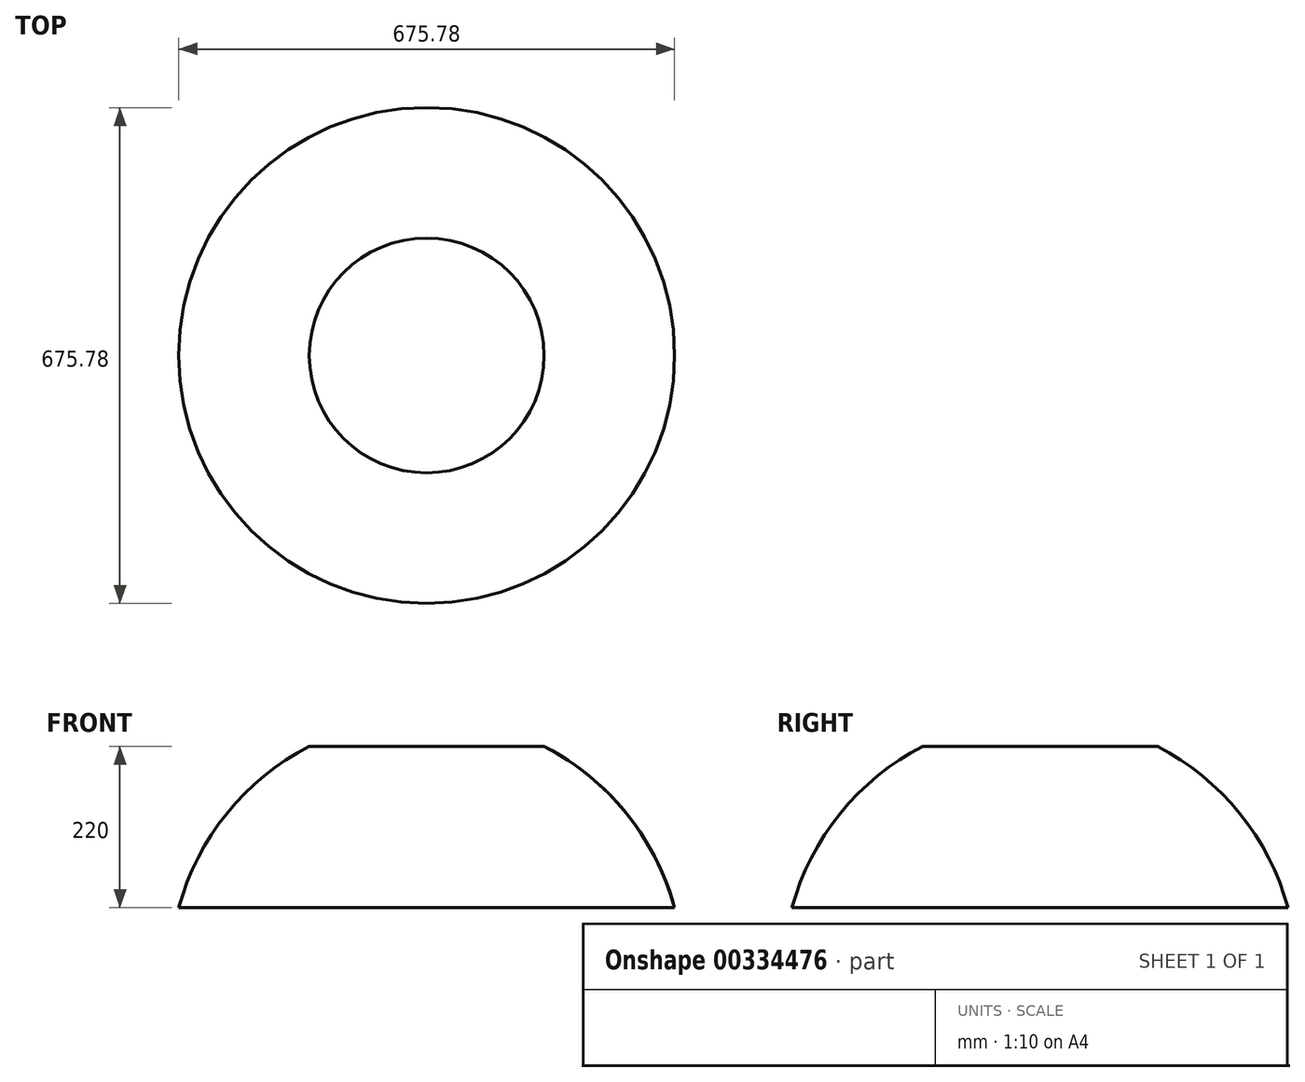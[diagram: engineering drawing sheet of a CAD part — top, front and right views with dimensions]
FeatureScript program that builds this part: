
annotation { "Feature Type Name" : "Feature", "Feature Type Description" : "" }
export const myFeature = defineFeature(function(context is Context, id is Id, definition is map)
    precondition{}
    {
        {
            var Q0;
            Q0=qCreatedBy(makeId("Front.planeOp"),FACE);
            var sketch = newSketch(context, id + "F0", { "sketchPlane" : qUnion([Q0])});
            skLineSegment(sketch, "E0", {"start": v(0, 246.6) * mm, "end": v(0, 0) * mm, "construction": true});
            skArc(sketch, "E1", {"start": v(-350, 0) * mm, "mid": v(0, 350) * mm, "end": v(350, 0) * mm});
            skLineSegment(sketch, "E2", {"start": v(-160, 311.29) * mm, "end": v(160, 311.29) * mm});
            skLineSegment(sketch, "E3", {"start": v(-337.89, 91.29) * mm, "end": v(337.89, 91.29) * mm});
            skLineSegment(sketch, "E4", {"start": v(0, 311.29) * mm, "end": v(0, 91.29) * mm});
            skSolve(sketch);
        }
        {
            var Q0;
            {var subQ5=sQuery(id+"F0.wireOp",EDGE,"E4");Q0=makeQuery(id+"F0.imprint","IMPRINT",FACE,{"disambiguationData":[TD([[makeQuery(id+"F0.imprint","IMPRINT",EDGE,{"derivedFrom":subQ5}),-1.0]])]});}
            var Q1;
            Q1=sQuery(id+"F0.wireOp",EDGE,"E4");
            revolve(context, id + "F1", {"entities" : qUnion([Q0]), "axis" : qUnion([Q1]), "revolveType" : RevolveType.FULL});
        }
    });
